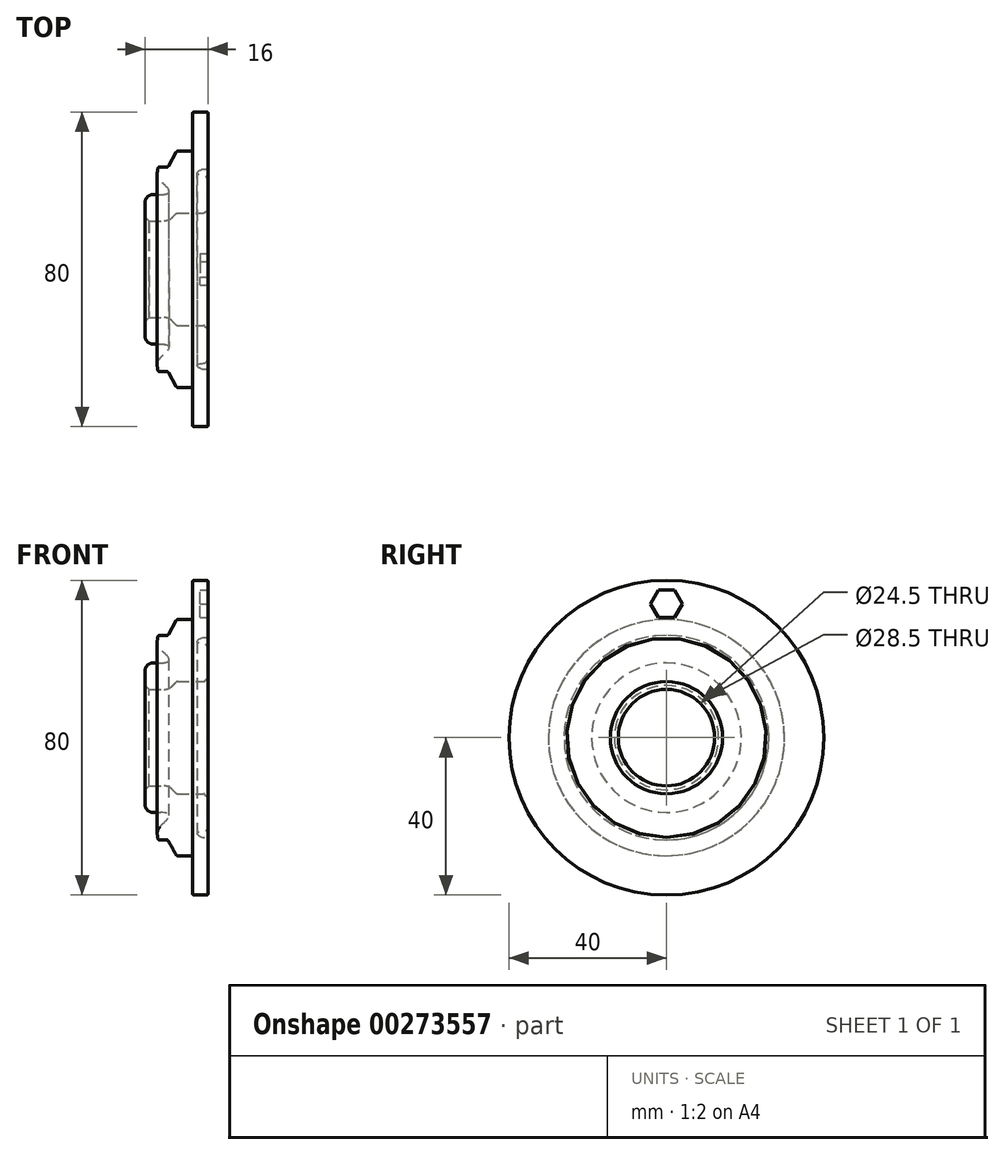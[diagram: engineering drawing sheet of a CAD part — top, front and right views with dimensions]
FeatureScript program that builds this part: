
annotation { "Feature Type Name" : "Feature", "Feature Type Description" : "" }
export const myFeature = defineFeature(function(context is Context, id is Id, definition is map)
    precondition{}
    {
        {
            var Q0;
            Q0=qCreatedBy(makeId("Front.planeOp"),FACE);
            var sketch = newSketch(context, id + "F0", { "sketchPlane" : qUnion([Q0])});
            skLineSegment(sketch, "E0", {"start": v(0, 0) * mm, "end": v(-16, 0) * mm});
            skLineSegment(sketch, "E1", {"start": v(-16, 0) * mm, "end": v(-16, 19) * mm});
            skLineSegment(sketch, "E2", {"start": v(-16, 19) * mm, "end": v(-12.1, 19) * mm});
            skLineSegment(sketch, "E3", {"start": v(0, 0) * mm, "end": v(0, 20.92) * mm});
            skFitSpline(sketch, "E4", {"points": [v(-12.69, 26) * mm, v(-11.57, 21.91) * mm, v(-12.1, 19) * mm], "startDerivative": vector(-2.48, -11.74) * mm, "endDerivative": vector(-25.36, 0) * mm});
            skLineSegment(sketch, "E5", {"start": v(-9, 0) * mm, "end": v(-9, 14.25) * mm});
            skLineSegment(sketch, "E6", {"start": v(-9, 14.25) * mm, "end": v(0, 14.25) * mm});
            skPoint(sketch, "E7", {"position": v(-6.48, 62.5) * mm});
            skPoint(sketch, "E8", {"position": v(-4.44, 28.36) * mm});
            skFitSpline(sketch, "E9", {"points": [v(0, 20.92) * mm, v(-1.36, 23.88) * mm, v(-2.83, 24.4) * mm, v(-1.17, 25.37) * mm, v(0, 30) * mm], "startDerivative": vector(0, 30.8) * mm, "endDerivative": vector(0, 53.38) * mm});
            skLineSegment(sketch, "E10", {"start": v(0, 40) * mm, "end": v(-4, 40) * mm});
            skLineSegment(sketch, "E11", {"start": v(-4, 40) * mm, "end": v(-4, 30) * mm});
            skLineSegment(sketch, "E12", {"start": v(-4, 30) * mm, "end": v(-8, 30) * mm});
            skLineSegment(sketch, "E13", {"start": v(-10.25, 26) * mm, "end": v(-8, 30) * mm});
            skLineSegment(sketch, "E14", {"start": v(-10.25, 26) * mm, "end": v(-12.69, 26) * mm});
            skLineSegment(sketch, "E15", {"start": v(0, 30) * mm, "end": v(0, 40) * mm});
            skLineSegment(sketch, "E16", {"start": v(-9, 12.25) * mm, "end": v(-16, 12.25) * mm});
            skSolve(sketch);
        }
        {
            var Q0;
            {var subQ5=sQuery(id+"F0.wireOp",EDGE,"E2");Q0=makeQuery(id+"F0.imprint","IMPRINT",FACE,{"disambiguationData":[TD([[makeQuery(id+"F0.imprint","IMPRINT",EDGE,{"derivedFrom":subQ5}),-1.0]])]});}
            var Q1;
            {var subQ0=sQuery(id+"F0.wireOp",EDGE,"HNAj4O2R-bTQW-l742-k01n-k4t6RiFG52qu");Q1=makeQuery(id+"F0.imprint","IMPRINT",FACE,{"disambiguationData":[TD([[makeQuery(id+"F0.imprint","IMPRINT",EDGE,{"derivedFrom":subQ0}),1.0]])]});}
            var Q2;
            {var subQ0=sQuery(id+"F0.wireOp",EDGE,"HNAj4O2R-bTQW-l742-k01n-k4t6RiFG52qu");Q2=makeQuery(id+"F0.imprint","IMPRINT",FACE,{"disambiguationData":[TD([[makeQuery(id+"F0.imprint","IMPRINT",EDGE,{"derivedFrom":subQ0}),-1.0]])]});}
            var Q3;
            Q3=sQuery(id+"F0.wireOp",EDGE,"E0");
            revolve(context, id + "F1", {"entities" : qUnion([Q0, Q1, Q2]), "axis" : qUnion([Q3]), "revolveType" : RevolveType.FULL});
        }
        {
            var Q0;
            Q0=makeQuery(id+"F1.opRevolve","SWEPT_EDGE",EDGE,{"disambiguationData":[OSD([sQuery(id+"F0.wireOp",EDGE,"E1"),sQuery(id+"F0.wireOp",EDGE,"E2")])]});
            fillet(context, id + "F2", {"entities" : qUnion([Q0]), "radius" : 2 * mm, "tangentPropagation" : true, "allowEdgeOverflow" : false});
        }
        {
            var Q0;
            Q0=makeQuery(id+"F1.opRevolve","SWEPT_EDGE",EDGE,{"disambiguationData":[OSD([sQuery(id+"F0.wireOp",EDGE,"E5"),sQuery(id+"F0.wireOp",EDGE,"g5jZlDZ4-7WYw-ZnNQ-leFQ-YIYegG46g59X")])]});
            chamfer(context, id + "F3", {"entities" : qUnion([Q0]), "width" : 1 * mm, "tangentPropagation" : true});
        }
        {
            var Q0;
            {var subQ0=sQuery(id+"F0.wireOp",EDGE,"E6");Q0=makeQuery(id+"F3.opChamfer","BLEND_EDGE",EDGE,{"blendedFrom":[makeQuery(id+"F1.opRevolve","SWEPT_EDGE",EDGE,{"disambiguationData":[OSD([sQuery(id+"F0.wireOp",EDGE,"E5"),subQ0])]}),makeQuery(id+"F1.opRevolve","SWEPT_FACE",FACE,{"disambiguationData":[OSD([subQ0])]})],"blendedInto":[makeQuery(id+"F1.opRevolve","SWEPT_FACE",FACE,{"disambiguationData":[OSD([subQ0])]})]});}
            fillet(context, id + "F4", {"entities" : qUnion([Q0]), "radius" : .5 * mm, "tangentPropagation" : true, "allowEdgeOverflow" : false});
        }
        {
            var Q0;
            Q0=makeQuery(id+"F1.opRevolve","SWEPT_EDGE",EDGE,{"disambiguationData":[OSD([sQuery(id+"F0.wireOp",EDGE,"E3"),sQuery(id+"F0.wireOp",EDGE,"E6")])]});
            chamfer(context, id + "F5", {"entities" : qUnion([Q0]), "width" : 1 * mm, "tangentPropagation" : true});
        }
        {
            var Q0;
            Q0=makeQuery(id+"F5.opChamfer","BLEND_FACE",FACE,{"disambiguationData":[OSD([sQuery(id+"F0.wireOp",EDGE,"E3"),sQuery(id+"F0.wireOp",EDGE,"E6")])]});
            var Q1;
            Q1=makeQuery(id+"F1.opRevolve","SWEPT_FACE",FACE,{"disambiguationData":[OSD([sQuery(id+"F0.wireOp",EDGE,"g5jZlDZ4-7WYw-ZnNQ-leFQ-YIYegG46g59X")])]});
            fillet(context, id + "F6", {"entities" : qUnion([Q0, Q1]), "radius" : .5 * mm, "tangentPropagation" : true, "allowEdgeOverflow" : false});
        }
        {
            var Q0;
            Q0=makeQuery(id+"F1.opRevolve","SWEPT_EDGE",EDGE,{"disambiguationData":[OSD([sQuery(id+"F0.wireOp",EDGE,"E1"),sQuery(id+"F0.wireOp",EDGE,"nIUL83w0-O1cN-WAI7-FeXO-9luYWBCx3RM4")])]});
            chamfer(context, id + "F7", {"entities" : qUnion([Q0]), "width" : 1 * mm, "tangentPropagation" : true});
        }
        {
            var Q0;
            Q0=makeQuery(id+"F1.opRevolve","SWEPT_FACE",FACE,{"disambiguationData":[OSD([sQuery(id+"F0.wireOp",EDGE,"E15")])]});
            var sketch = newSketch(context, id + "F8", { "sketchPlane" : qUnion([Q0])});
            skCircle(sketch, "E17.cCircle", {"center": v(0, 34) * mm, "radius": 3.5 * mm, "construction": true});
            skLineSegment(sketch, "E17.0", {"start": v(-4.03, 34) * mm, "end": v(-2.02, 37.48) * mm});
            skLineSegment(sketch, "E17.1", {"start": v(-2.02, 37.48) * mm, "end": v(2.02, 37.48) * mm});
            skLineSegment(sketch, "E17.2", {"start": v(2.02, 37.48) * mm, "end": v(4.03, 34) * mm});
            skLineSegment(sketch, "E17.3", {"start": v(4.03, 34) * mm, "end": v(2.02, 30.5) * mm});
            skLineSegment(sketch, "E17.4", {"start": v(2.02, 30.5) * mm, "end": v(-2.02, 30.5) * mm});
            skLineSegment(sketch, "E17.5", {"start": v(-2.02, 30.5) * mm, "end": v(-4.03, 34) * mm});
            skPoint(sketch, "E17.0.midPoint", {"position": v(-3.02, 35.74) * mm});
            skSolve(sketch);
        }
        {
            var Q0;
            Q0 = qSketchRegion(id + "F8", true);
            extrude(context, id + "F9", {"entities" : qUnion([Q0]), "operationType" : NewBodyOperationType.REMOVE, "oppositeDirection" : true, "depth" : 2 * mm});
        }
        {
            var Q0;
            {var subQ0=sQuery(id+"F0.wireOp",EDGE,"E16");Q0=makeQuery(id+"F3.opChamfer","BLEND_EDGE",EDGE,{"blendedFrom":[makeQuery(id+"F1.opRevolve","SWEPT_EDGE",EDGE,{"disambiguationData":[OSD([sQuery(id+"F0.wireOp",EDGE,"E5"),subQ0])]}),makeQuery(id+"F1.opRevolve","SWEPT_FACE",FACE,{"disambiguationData":[OSD([subQ0])]})],"blendedInto":[makeQuery(id+"F1.opRevolve","SWEPT_FACE",FACE,{"disambiguationData":[OSD([subQ0])]})]});}
            fillet(context, id + "F10", {"entities" : qUnion([Q0]), "radius" : 3 * mm, "tangentPropagation" : true, "allowEdgeOverflow" : false});
        }
        {
            var Q0;
            Q0=makeQuery(id+"F1.opRevolve","SWEPT_FACE",FACE,{"disambiguationData":[OSD([sQuery(id+"F0.wireOp",EDGE,"E10")])]});
            var Q1;
            Q1=makeQuery(id+"F1.opRevolve","SWEPT_FACE",FACE,{"disambiguationData":[OSD([sQuery(id+"F0.wireOp",EDGE,"E13")])]});
            var Q2;
            Q2=makeQuery(id+"F1.opRevolve","SWEPT_FACE",FACE,{"disambiguationData":[OSD([sQuery(id+"F0.wireOp",EDGE,"E14")])]});
            fillet(context, id + "F11", {"entities" : qUnion([Q0, Q1, Q2]), "radius" : .5 * mm, "tangentPropagation" : true, "allowEdgeOverflow" : false});
        }
    });
